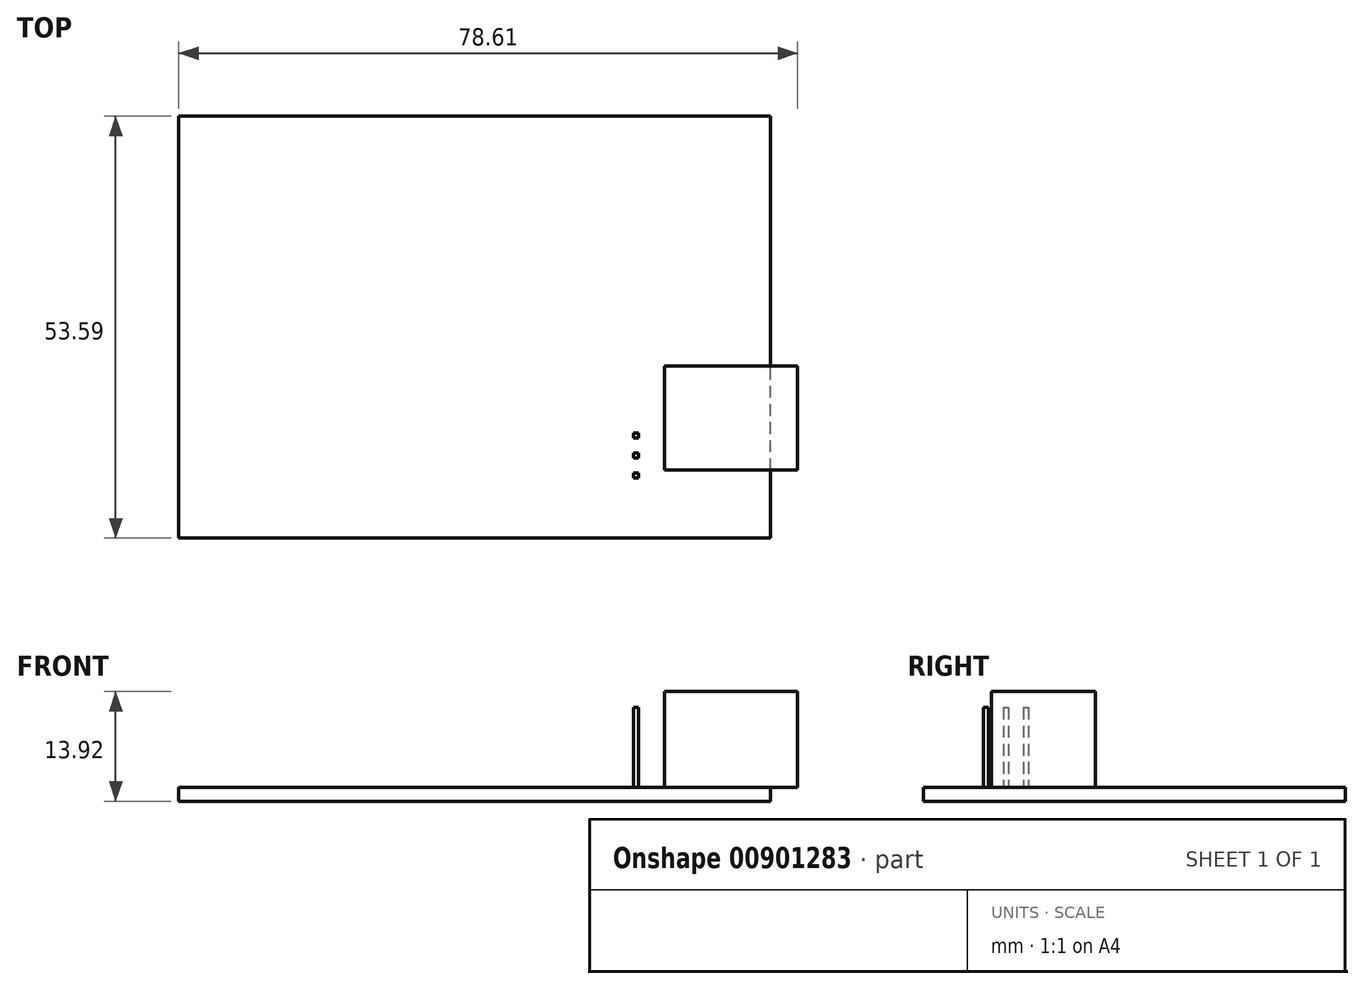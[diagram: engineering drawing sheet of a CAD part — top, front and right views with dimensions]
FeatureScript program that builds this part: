
annotation { "Feature Type Name" : "Feature", "Feature Type Description" : "" }
export const myFeature = defineFeature(function(context is Context, id is Id, definition is map)
    precondition{}
    {
        {
            var Q0;
            Q0=qCreatedBy(makeId("Top.planeOp"),FACE);
            var sketch = newSketch(context, id + "F0", { "sketchPlane" : qUnion([Q0])});
            skLineSegment(sketch, "E0.bottom", {"start": v(0, 0) * mm, "end": v(75.18, 0) * mm});
            skLineSegment(sketch, "E0.top", {"start": v(0, 53.6) * mm, "end": v(75.18, 53.6) * mm});
            skLineSegment(sketch, "E0.left", {"start": v(0, 0) * mm, "end": v(0, 53.6) * mm});
            skLineSegment(sketch, "E0.right", {"start": v(75.18, 0) * mm, "end": v(75.18, 53.6) * mm});
            skSolve(sketch);
        }
        {
            var Q0;
            Q0 = qSketchRegion(id + "F0", true);
            extrude(context, id + "F1", {"entities" : qUnion([Q0]), "depth" : 1.73 * mm, "offsetDistance" : 25.4 * mm});
        }
        {
            var Q0;
            Q0=makeQuery(id+"F1.opExtrude","CAP_FACE",FACE,{"disambiguationData":[OSD([sQuery(id+"F0.wireOp",EDGE,"E0.bottom"),sQuery(id+"F0.wireOp",EDGE,"E0.top"),sQuery(id+"F0.wireOp",EDGE,"E0.left"),sQuery(id+"F0.wireOp",EDGE,"E0.right")])],"isStart":false});
            var sketch = newSketch(context, id + "F2", { "sketchPlane" : qUnion([Q0])});
            skLineSegment(sketch, "E1.bottom", {"start": v(61.72, 8.64) * mm, "end": v(78.61, 8.64) * mm});
            skLineSegment(sketch, "E1.top", {"start": v(61.72, 21.84) * mm, "end": v(78.61, 21.84) * mm});
            skLineSegment(sketch, "E1.left", {"start": v(61.72, 8.64) * mm, "end": v(61.72, 21.84) * mm});
            skLineSegment(sketch, "E1.right", {"start": v(78.61, 8.64) * mm, "end": v(78.61, 21.84) * mm});
            skSolve(sketch);
        }
        {
            var Q0;
            Q0 = qSketchRegion(id + "F2", true);
            extrude(context, id + "F3", {"entities" : qUnion([Q0]), "operationType" : NewBodyOperationType.ADD, "depth" : 12.2 * mm, "offsetDistance" : 25.4 * mm});
        }
        {
            var Q0;
            Q0=makeQuery(id+"F1.opExtrude","CAP_FACE",FACE,{"disambiguationData":[OSD([sQuery(id+"F0.wireOp",EDGE,"E0.bottom"),sQuery(id+"F0.wireOp",EDGE,"E0.top"),sQuery(id+"F0.wireOp",EDGE,"E0.left"),sQuery(id+"F0.wireOp",EDGE,"E0.right")])],"isStart":false});
            var sketch = newSketch(context, id + "F4", { "sketchPlane" : qUnion([Q0])});
            skLineSegment(sketch, "E2.bottom", {"start": v(57.79, 7.62) * mm, "end": v(58.42, 7.62) * mm});
            skLineSegment(sketch, "E2.top", {"start": v(57.79, 8.26) * mm, "end": v(58.42, 8.26) * mm});
            skLineSegment(sketch, "E2.left", {"start": v(57.79, 7.62) * mm, "end": v(57.79, 8.26) * mm});
            skLineSegment(sketch, "E2.right", {"start": v(58.42, 7.62) * mm, "end": v(58.42, 8.26) * mm});
            skLineSegment(sketch, "E3.0.1.0", {"start": v(58.42, 10.16) * mm, "end": v(58.42, 10.8) * mm});
            skLineSegment(sketch, "E3.0.1.1", {"start": v(57.79, 10.8) * mm, "end": v(58.42, 10.8) * mm});
            skLineSegment(sketch, "E3.0.1.2", {"start": v(57.79, 10.16) * mm, "end": v(58.42, 10.16) * mm});
            skLineSegment(sketch, "E3.0.1.3", {"start": v(57.79, 10.16) * mm, "end": v(57.79, 10.8) * mm});
            skLineSegment(sketch, "E3.0.2.0", {"start": v(58.42, 12.7) * mm, "end": v(58.42, 13.34) * mm});
            skLineSegment(sketch, "E3.0.2.1", {"start": v(57.79, 13.34) * mm, "end": v(58.42, 13.34) * mm});
            skLineSegment(sketch, "E3.0.2.2", {"start": v(57.79, 12.7) * mm, "end": v(58.42, 12.7) * mm});
            skLineSegment(sketch, "E3.0.2.3", {"start": v(57.79, 12.7) * mm, "end": v(57.79, 13.34) * mm});
            skLineSegment(sketch, "E3.direction1", {"start": v(57.79, 7.62) * mm, "end": v(63.42, 7.62) * mm, "construction": true});
            skLineSegment(sketch, "E3.direction2", {"start": v(57.79, 7.62) * mm, "end": v(57.79, 10.16) * mm, "construction": true});
            skSolve(sketch);
        }
        {
            var Q0;
            Q0 = qSketchRegion(id + "F4", true);
            extrude(context, id + "F5", {"entities" : qUnion([Q0]), "operationType" : NewBodyOperationType.ADD, "depth" : 10.16 * mm, "offsetDistance" : 25.4 * mm});
        }
    });
